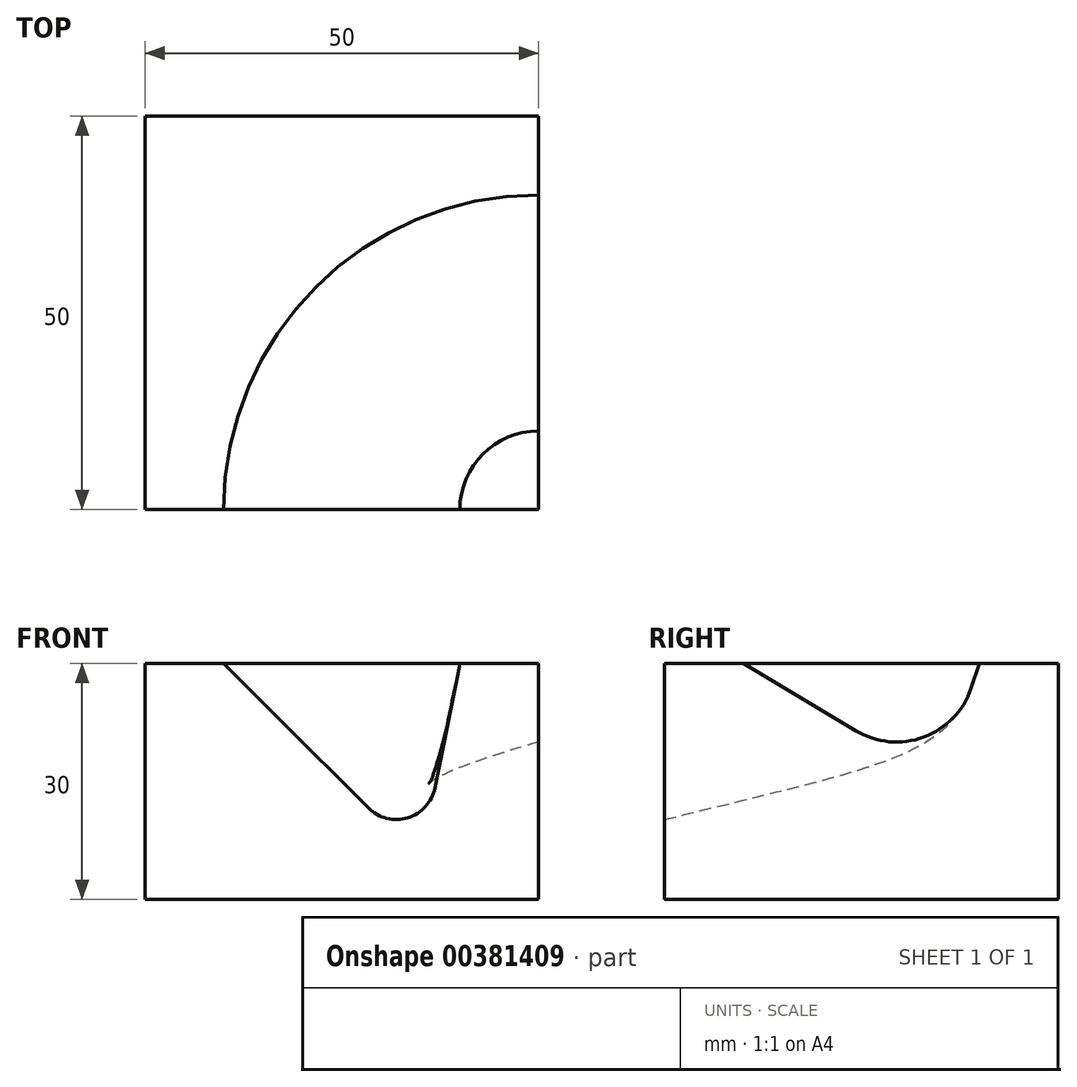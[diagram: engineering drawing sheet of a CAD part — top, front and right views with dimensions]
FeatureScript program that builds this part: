
annotation { "Feature Type Name" : "Feature", "Feature Type Description" : "" }
export const myFeature = defineFeature(function(context is Context, id is Id, definition is map)
    precondition{}
    {
        {
            var Q0;
            Q0=qCreatedBy(makeId("Top.planeOp"),FACE);
            var sketch = newSketch(context, id + "F0", { "sketchPlane" : qUnion([Q0])});
            skLineSegment(sketch, "E0.bottom", {"start": v(25, -25) * mm, "end": v(-25, -25) * mm});
            skLineSegment(sketch, "E0.top", {"start": v(25, 25) * mm, "end": v(-25, 25) * mm});
            skLineSegment(sketch, "E0.left", {"start": v(25, -25) * mm, "end": v(25, 25) * mm});
            skLineSegment(sketch, "E0.right", {"start": v(-25, -25) * mm, "end": v(-25, 25) * mm});
            skPoint(sketch, "E0.middle", {"position": v(0, 0) * mm});
            skSolve(sketch);
        }
        {
            var Q0;
            Q0=makeQuery(id+"F0.imprint","IMPRINT",FACE,{"disambiguationData":[TD([[makeQuery(id+"F0.imprint","IMPRINT",EDGE,{"derivedFrom":sQuery(id+"F0.wireOp",EDGE,"E0.bottom")}),-1.0]])]});
            extrude(context, id + "F1", {"entities" : qUnion([Q0]), "depth" : 30 * mm});
        }
        {
            var Q0;
            Q0=makeQuery(id+"F1.opExtrude","CAP_FACE",FACE,{"disambiguationData":[OSD([sQuery(id+"F0.wireOp",EDGE,"E0.bottom"),sQuery(id+"F0.wireOp",EDGE,"E0.top"),sQuery(id+"F0.wireOp",EDGE,"E0.left"),sQuery(id+"F0.wireOp",EDGE,"E0.right")])],"isStart":false});
            var sketch = newSketch(context, id + "F2", { "sketchPlane" : qUnion([Q0])});
            skArc(sketch, "E1", {"start": v(25, 15) * mm, "mid": v(-3.28, 3.28) * mm, "end": v(-15, -25) * mm});
            skArc(sketch, "E2", {"start": v(25, -15) * mm, "mid": v(17.93, -17.93) * mm, "end": v(15, -25) * mm});
            skSolve(sketch);
        }
        {
            var Q0;
            Q0=makeQuery(id+"F1.opExtrude","SWEPT_FACE",FACE,{"disambiguationData":[OSD([sQuery(id+"F0.wireOp",EDGE,"E0.bottom")])]});
            var sketch = newSketch(context, id + "F3", { "sketchPlane" : qUnion([Q0])});
            skLineSegment(sketch, "E3", {"start": v(-15, 30) * mm, "end": v(3.4, 11.6) * mm});
            skLineSegment(sketch, "E4", {"start": v(11.83, 14.16) * mm, "end": v(15, 30) * mm});
            skPoint(sketch, "E5.visualSharp", {"position": v(10, 5) * mm});
            skArc(sketch, "E5.filletArc", {"start": v(3.4, 11.6) * mm, "mid": v(8.38, 10.36) * mm, "end": v(11.83, 14.16) * mm});
            skSolve(sketch);
        }
        {
            var Q0;
            Q0=makeQuery(id+"F1.opExtrude","SWEPT_FACE",FACE,{"disambiguationData":[OSD([sQuery(id+"F0.wireOp",EDGE,"E0.left")])]});
            var sketch = newSketch(context, id + "F4", { "sketchPlane" : qUnion([Q0])});
            skLineSegment(sketch, "E6", {"start": v(-15, 30) * mm, "end": v(-0.69, 21.41) * mm});
            skLineSegment(sketch, "E7", {"start": v(13.94, 26.83) * mm, "end": v(15, 30) * mm});
            skPoint(sketch, "E8.visualSharp", {"position": v(10, 15) * mm});
            skArc(sketch, "E8.filletArc", {"start": v(-0.69, 21.41) * mm, "mid": v(7.92, 20.6) * mm, "end": v(13.94, 26.83) * mm});
            skSolve(sketch);
        }
        {
            var Q1;
            {var subQ0=sQuery(id+"F3.wireOp",EDGE,"E3");Q1=makeQuery(id+"F3.imprint","IMPRINT",FACE,{"disambiguationData":[TD([[makeQuery(id+"F3.imprint","IMPRINT",EDGE,{"derivedFrom":subQ0}),1.0]])]});}
            var Q2;
            {var subQ0=sQuery(id+"F4.wireOp",EDGE,"E6");Q2=makeQuery(id+"F4.imprint","IMPRINT",FACE,{"disambiguationData":[TD([[makeQuery(id+"F4.imprint","IMPRINT",EDGE,{"derivedFrom":subQ0}),1.0]])]});}
            var Q3;
            Q3=sQuery(id+"F2.wireOp",EDGE,"E1");
            var Q4;
            Q4=sQuery(id+"F2.wireOp",EDGE,"E2");
            loft(context, id + "F5", {"operationType" : NewBodyOperationType.REMOVE, "addGuides" : true, "sheetProfilesArray" : [{ "sheetProfileEntities" : qUnion([Q1]) }, { "sheetProfileEntities" : qUnion([Q2]) }], "guidesArray" : [{ "guideEntities" : qUnion([Q3]), "guideDerivativeType" : LoftGuideDerivativeType.DEFAULT, "guideDerivativeMagnitude" : 1 }, { "guideEntities" : qUnion([Q4]), "guideDerivativeType" : LoftGuideDerivativeType.DEFAULT, "guideDerivativeMagnitude" : 1 }]});
        }
    });
